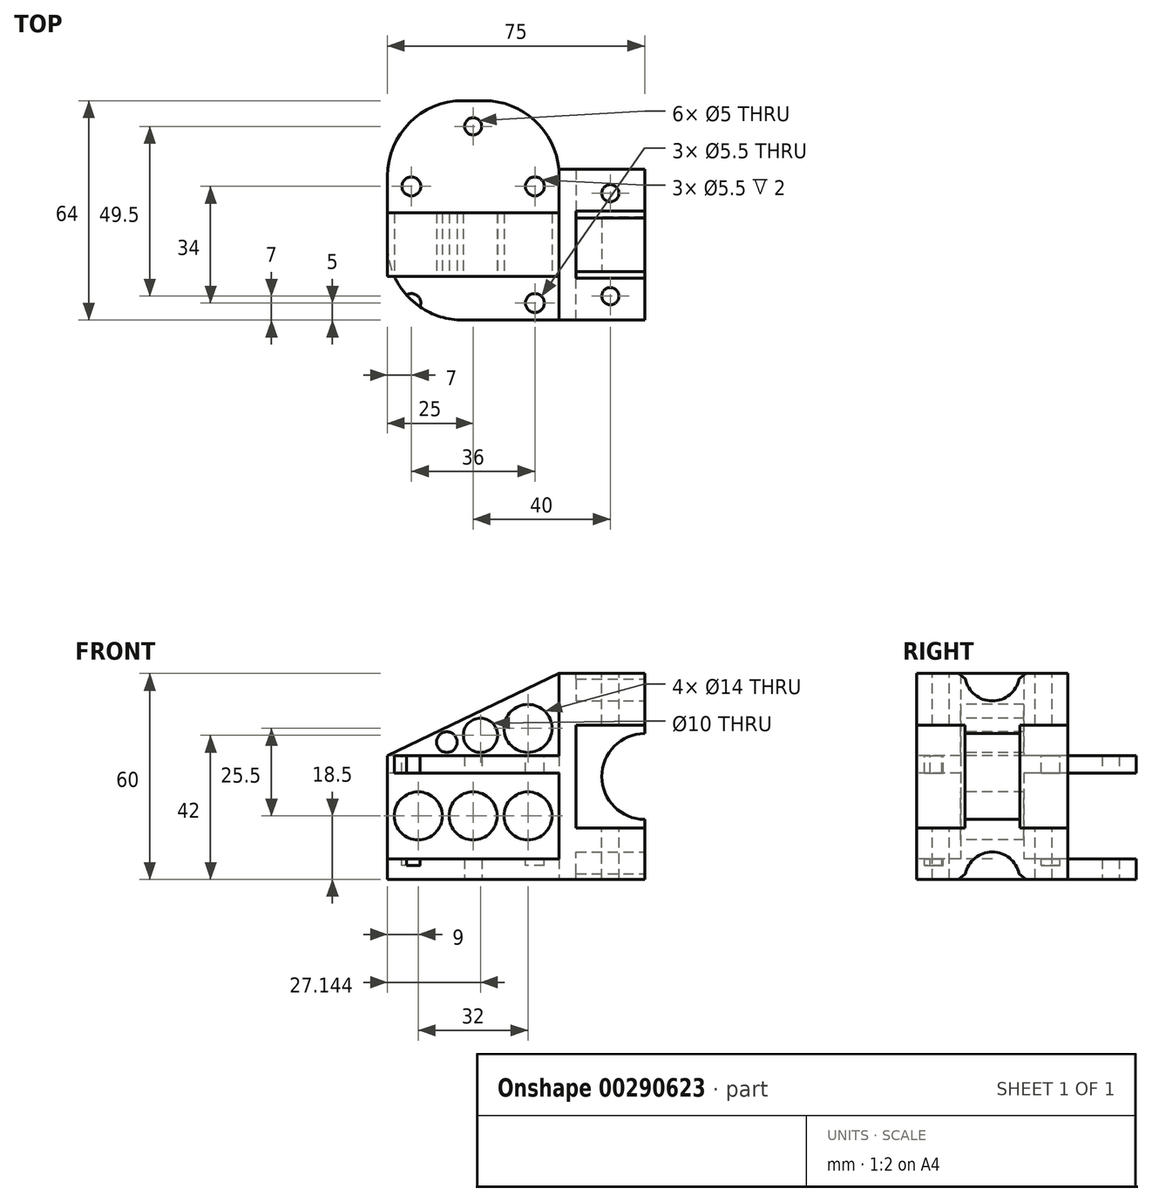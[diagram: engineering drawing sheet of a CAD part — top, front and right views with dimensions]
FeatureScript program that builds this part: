
annotation { "Feature Type Name" : "Feature", "Feature Type Description" : "" }
export const myFeature = defineFeature(function(context is Context, id is Id, definition is map)
    precondition{}
    {
        {
            var Q0;
            Q0=qCreatedBy(makeId("Top.planeOp"),FACE);
            var sketch = newSketch(context, id + "F0", { "sketchPlane" : qUnion([Q0])});
            skLineSegment(sketch, "E0.bottom", {"start": v(-25, 22) * mm, "end": v(25, 22) * mm});
            skLineSegment(sketch, "E0.top", {"start": v(-25, -22) * mm, "end": v(25, -22) * mm});
            skLineSegment(sketch, "E0.left", {"start": v(-25, 22) * mm, "end": v(-25, -22) * mm});
            skLineSegment(sketch, "E0.right", {"start": v(25, 22) * mm, "end": v(25, -22) * mm});
            skLineSegment(sketch, "E1.bottom", {"start": v(25, 22) * mm, "end": v(50, 22) * mm});
            skLineSegment(sketch, "E1.top", {"start": v(25, -22) * mm, "end": v(50, -22) * mm});
            skLineSegment(sketch, "E1.right", {"start": v(50, 22) * mm, "end": v(50, -22) * mm});
            skLineSegment(sketch, "E2", {"start": v(0, 22) * mm, "end": v(0, -22) * mm, "construction": true});
            skLineSegment(sketch, "E3", {"start": v(-25, 0) * mm, "end": v(25, 0) * mm, "construction": true});
            skPoint(sketch, "E4.center.orphan", {"position": v(0, -12) * mm});
            skLineSegment(sketch, "E5.bottom", {"start": v(25, -22) * mm, "end": v(-25, -22) * mm});
            skLineSegment(sketch, "E5.top", {"start": v(25, -42) * mm, "end": v(-25, -42) * mm});
            skLineSegment(sketch, "E5.left", {"start": v(25, -22) * mm, "end": v(25, -42) * mm});
            skLineSegment(sketch, "E5.right", {"start": v(-25, -22) * mm, "end": v(-25, -42) * mm});
            skLineSegment(sketch, "E6.top", {"start": v(-25, 42) * mm, "end": v(25, 42) * mm});
            skLineSegment(sketch, "E6.left", {"start": v(-25, 22) * mm, "end": v(-25, 42) * mm});
            skLineSegment(sketch, "E6.right", {"start": v(25, 22) * mm, "end": v(25, 42) * mm});
            skLineSegment(sketch, "E7", {"start": v(-25, -32) * mm, "end": v(25, -32) * mm, "construction": true});
            skLineSegment(sketch, "E8", {"start": v(0, -22) * mm, "end": v(0, -42) * mm, "construction": true});
            skLineSegment(sketch, "E9", {"start": v(0, 22) * mm, "end": v(0, 42) * mm, "construction": true});
            skLineSegment(sketch, "E10", {"start": v(-25, 32) * mm, "end": v(25, 32) * mm, "construction": true});
            skCircle(sketch, "E11", {"center": v(0, -34.5) * mm, "radius": 2.5 * mm});
            skCircle(sketch, "E12", {"center": v(0, 34.5) * mm, "radius": 2.5 * mm});
            skSolve(sketch);
        }
        {
            var Q0;
            Q0=makeQuery(id+"F0.imprint","IMPRINT",FACE,{"disambiguationData":[TD([[makeQuery(id+"F0.imprint","IMPRINT",EDGE,{"derivedFrom":sQuery(id+"F0.wireOp",EDGE,"E1.bottom")}),-1.0]])]});
            extrude(context, id + "F1", {"entities" : qUnion([Q0]), "depth" : 60 * mm});
        }
        {
            var Q0;
            {var subQ1=sQuery(id+"F0.wireOp",EDGE,"E0.bottom");Q0=makeQuery(id+"F0.imprint","IMPRINT",FACE,{"disambiguationData":[TD([[makeQuery(id+"F0.imprint","IMPRINT",EDGE,{"derivedFrom":subQ1}),-1.0]])]});}
            var Q1;
            Q1=makeQuery(id+"F0.imprint","IMPRINT",FACE,{"disambiguationData":[TD([[makeQuery(id+"F0.imprint","IMPRINT",EDGE,{"derivedFrom":sQuery(id+"F0.wireOp",EDGE,"E0.bottom")}),1.0]])]});
            var Q2;
            Q2=makeQuery(id+"F0.imprint","IMPRINT",FACE,{"disambiguationData":[TD([[makeQuery(id+"F0.imprint","IMPRINT",EDGE,{"derivedFrom":sQuery(id+"F0.wireOp",EDGE,"E5.bottom")}),1.0]])]});
            var Q3;
            Q3=makeQuery(id+"F0.imprint","IMPRINT",FACE,{"disambiguationData":[TD([[makeQuery(id+"F0.imprint","IMPRINT",EDGE,{"derivedFrom":sQuery(id+"F0.wireOp",EDGE,"E0.left")}),1.0]])]});
            extrude(context, id + "F2", {"entities" : qUnion([Q0, Q1, Q2, Q3]), "operationType" : NewBodyOperationType.ADD, "depth" : 6 * mm});
        }
        {
            var Q0;
            Q0=makeQuery(id+"F1.opExtrude","SWEPT_FACE",FACE,{"disambiguationData":[OSD([sQuery(id+"F0.wireOp",EDGE,"E1.right")])]});
            var sketch = newSketch(context, id + "F3", { "sketchPlane" : qUnion([Q0])});
            skCircle(sketch, "E13", {"center": v(0, 0) * mm, "radius": 8 * mm});
            skCircle(sketch, "E14", {"center": v(0, 60) * mm, "radius": 8 * mm});
            skSolve(sketch);
        }
        {
            var Q0;
            Q0 = qSketchRegion(id + "F3", true);
            extrude(context, id + "F4", {"entities" : qUnion([Q0]), "operationType" : NewBodyOperationType.REMOVE, "oppositeDirection" : true, "depth" : 20 * mm});
        }
        {
            var Q0;
            Q0=makeQuery(id+"F1.opExtrude","CAP_FACE",FACE,{"disambiguationData":[OSD([sQuery(id+"F0.wireOp",EDGE,"E1.bottom"),sQuery(id+"F0.wireOp",EDGE,"E1.top"),sQuery(id+"F0.wireOp",EDGE,"E0.right"),sQuery(id+"F0.wireOp",EDGE,"E1.right")])],"isStart":false});
            var sketch = newSketch(context, id + "F5", { "sketchPlane" : qUnion([Q0])});
            skLineSegment(sketch, "E15.bottom", {"start": v(50, 22) * mm, "end": v(30, 22) * mm, "construction": true});
            skLineSegment(sketch, "E15.top", {"start": v(50, -22) * mm, "end": v(30, -22) * mm, "construction": true});
            skLineSegment(sketch, "E15.left", {"start": v(50, 22) * mm, "end": v(50, -22) * mm, "construction": true});
            skLineSegment(sketch, "E15.right", {"start": v(30, 22) * mm, "end": v(30, 8) * mm, "construction": true});
            skLineSegment(sketch, "E16", {"start": v(40, 22) * mm, "end": v(40, 8) * mm, "construction": true});
            skLineSegment(sketch, "E17", {"start": v(30, 8) * mm, "end": v(50, 8) * mm, "construction": true});
            skLineSegment(sketch, "E18", {"start": v(30, -8) * mm, "end": v(50, -8) * mm, "construction": true});
            skLineSegment(sketch, "E19.trimOffspring", {"start": v(40, -8) * mm, "end": v(40, -22) * mm, "construction": true});
            skLineSegment(sketch, "E20.trimOffspring", {"start": v(30, -8) * mm, "end": v(30, -22) * mm, "construction": true});
            skLineSegment(sketch, "E21", {"start": v(30, 15) * mm, "end": v(50, 15) * mm, "construction": true});
            skLineSegment(sketch, "E22", {"start": v(30, -15) * mm, "end": v(50, -15) * mm, "construction": true});
            skCircle(sketch, "E23", {"center": v(40, 15) * mm, "radius": 2.5 * mm});
            skCircle(sketch, "E24", {"center": v(40, -15) * mm, "radius": 2.5 * mm});
            skSolve(sketch);
        }
        {
            var Q0;
            Q0 = qSketchRegion(id + "F5", true);
            extrude(context, id + "F6", {"entities" : qUnion([Q0]), "operationType" : NewBodyOperationType.REMOVE, "oppositeDirection" : true, "depth" : 60 * mm});
        }
        {
            var Q0;
            Q0=makeQuery(id+"F1.opExtrude","SWEPT_FACE",FACE,{"disambiguationData":[OSD([sQuery(id+"F0.wireOp",EDGE,"E1.right")])]});
            var sketch = newSketch(context, id + "F7", { "sketchPlane" : qUnion([Q0])});
            skLineSegment(sketch, "E25.bottom", {"start": v(22, 30) * mm, "end": v(-22, 30) * mm, "construction": true});
            skLineSegment(sketch, "E25.top", {"start": v(22, 30) * mm, "end": v(-22, 30) * mm, "construction": true});
            skLineSegment(sketch, "E25.left", {"start": v(22, 30) * mm, "end": v(22, 30) * mm});
            skLineSegment(sketch, "E25.right", {"start": v(-22, 30) * mm, "end": v(-22, 30) * mm});
            skLineSegment(sketch, "E26.bottom", {"start": v(-22, 45) * mm, "end": v(-8, 45) * mm});
            skLineSegment(sketch, "E26.top", {"start": v(-22, 15) * mm, "end": v(-8, 15) * mm});
            skLineSegment(sketch, "E26.left", {"start": v(-22, 45) * mm, "end": v(-22, 15) * mm});
            skLineSegment(sketch, "E26.right", {"start": v(-8, 45) * mm, "end": v(-8, 15) * mm});
            skLineSegment(sketch, "E27.bottom", {"start": v(22, 45) * mm, "end": v(8, 45) * mm});
            skLineSegment(sketch, "E27.top", {"start": v(22, 15) * mm, "end": v(8, 15) * mm});
            skLineSegment(sketch, "E27.left", {"start": v(22, 45) * mm, "end": v(22, 15) * mm});
            skLineSegment(sketch, "E27.right", {"start": v(8, 45) * mm, "end": v(8, 15) * mm});
            skSolve(sketch);
        }
        {
            var Q0;
            Q0 = qSketchRegion(id + "F7", true);
            extrude(context, id + "F8", {"entities" : qUnion([Q0]), "operationType" : NewBodyOperationType.REMOVE, "oppositeDirection" : true, "depth" : 20 * mm});
        }
        {
            var Q0;
            Q0=makeQuery(id+"F2.opExtrude","CAP_FACE",FACE,{"disambiguationData":[OSD([sQuery(id+"F0.wireOp",EDGE,"E0.bottom"),sQuery(id+"F0.wireOp",EDGE,"E0.top"),sQuery(id+"F0.wireOp",EDGE,"E0.left"),sQuery(id+"F0.wireOp",EDGE,"E0.right"),sQuery(id+"F0.wireOp",EDGE,"CU1M1yZN-sxm3-3OR8-gPQy-L78A4Of9dSzU"),sQuery(id+"F0.wireOp",EDGE,"da8ced7d-3d86-45b0-b41d-8282a98df76d0.MirrorC")])],"isStart":false});
            extrude(context, id + "F9", {"entities" : qUnion([Q0]), "operationType" : NewBodyOperationType.ADD, "depth" : 30 * mm, "hasSecondDirection" : true, "secondDirectionOppositeDirection" : false, "secondDirectionDepth" : 25 * mm});
        }
        {
            var Q0;
            Q0=makeQuery(id+"F9.opExtrude","SWEPT_EDGE",EDGE,{"disambiguationData":[OSD([sQuery(id+"F0.wireOp",EDGE,"E5.top"),sQuery(id+"F0.wireOp",EDGE,"E5.left")])]});
            var Q1;
            Q1=makeQuery(id+"F2.opExtrude","SWEPT_EDGE",EDGE,{"disambiguationData":[OSD([sQuery(id+"F0.wireOp",EDGE,"E5.top"),sQuery(id+"F0.wireOp",EDGE,"E5.left")])]});
            var Q2;
            Q2=makeQuery(id+"F2.opExtrude","SWEPT_EDGE",EDGE,{"disambiguationData":[OSD([sQuery(id+"F0.wireOp",EDGE,"E5.top"),sQuery(id+"F0.wireOp",EDGE,"E5.right")])]});
            var Q3;
            Q3=makeQuery(id+"F9.opExtrude","SWEPT_EDGE",EDGE,{"disambiguationData":[OSD([sQuery(id+"F0.wireOp",EDGE,"E5.top"),sQuery(id+"F0.wireOp",EDGE,"E5.right")])]});
            var Q4;
            Q4=makeQuery(id+"F9.opExtrude","SWEPT_EDGE",EDGE,{"disambiguationData":[OSD([sQuery(id+"F0.wireOp",EDGE,"E6.top"),sQuery(id+"F0.wireOp",EDGE,"E6.left")])]});
            var Q5;
            Q5=makeQuery(id+"F2.opExtrude","SWEPT_EDGE",EDGE,{"disambiguationData":[OSD([sQuery(id+"F0.wireOp",EDGE,"E6.top"),sQuery(id+"F0.wireOp",EDGE,"E6.left")])]});
            var Q6;
            Q6=makeQuery(id+"F9.opExtrude","SWEPT_EDGE",EDGE,{"disambiguationData":[OSD([sQuery(id+"F0.wireOp",EDGE,"E6.top"),sQuery(id+"F0.wireOp",EDGE,"E6.right")])]});
            var Q7;
            Q7=makeQuery(id+"F2.opExtrude","SWEPT_EDGE",EDGE,{"disambiguationData":[OSD([sQuery(id+"F0.wireOp",EDGE,"E6.top"),sQuery(id+"F0.wireOp",EDGE,"E6.right")])]});
            fillet(context, id + "F10", {"entities" : qUnion([Q0, Q1, Q2, Q3, Q4, Q5, Q6, Q7]), "radius" : 22 * mm, "tangentPropagation" : true, "allowEdgeOverflow" : false});
        }
        {
            var Q0;
            Q0=makeQuery(id+"F9.opExtrude","CAP_FACE",FACE,{"disambiguationData":[OSD([sQuery(id+"F0.wireOp",EDGE,"E0.left"),sQuery(id+"F0.wireOp",EDGE,"E0.right"),sQuery(id+"F0.wireOp",EDGE,"E5.top"),sQuery(id+"F0.wireOp",EDGE,"E5.left"),sQuery(id+"F0.wireOp",EDGE,"E5.right"),sQuery(id+"F0.wireOp",EDGE,"E6.top"),sQuery(id+"F0.wireOp",EDGE,"E6.left"),sQuery(id+"F0.wireOp",EDGE,"E6.right"),sQuery(id+"F0.wireOp",EDGE,"E11"),sQuery(id+"F0.wireOp",EDGE,"E12")])],"isStart":false});
            var sketch = newSketch(context, id + "F11", { "sketchPlane" : qUnion([Q0])});
            skCircle(sketch, "E28", {"center": v(18, 17) * mm, "radius": 2.75 * mm});
            skCircle(sketch, "E29.MirrorC", {"center": v(-18, 17) * mm, "radius": 2.75 * mm});
            skCircle(sketch, "E30.MirrorC", {"center": v(-18, -17) * mm, "radius": 2.75 * mm});
            skCircle(sketch, "E31.MirrorC", {"center": v(18, -17) * mm, "radius": 2.75 * mm});
            skSolve(sketch);
        }
        {
            var Q0;
            Q0 = qSketchRegion(id + "F11", true);
            extrude(context, id + "F12", {"entities" : qUnion([Q0]), "operationType" : NewBodyOperationType.REMOVE, "oppositeDirection" : true, "depth" : 32 * mm});
        }
        {
            var Q0;
            Q0=makeQuery(id+"F2.opExtrude","CAP_FACE",FACE,{"disambiguationData":[OSD([sQuery(id+"F0.wireOp",EDGE,"E0.left"),sQuery(id+"F0.wireOp",EDGE,"E0.right"),sQuery(id+"F0.wireOp",EDGE,"E5.top"),sQuery(id+"F0.wireOp",EDGE,"E5.left"),sQuery(id+"F0.wireOp",EDGE,"E5.right"),sQuery(id+"F0.wireOp",EDGE,"E6.top"),sQuery(id+"F0.wireOp",EDGE,"E6.left"),sQuery(id+"F0.wireOp",EDGE,"E6.right"),sQuery(id+"F0.wireOp",EDGE,"E11"),sQuery(id+"F0.wireOp",EDGE,"E12")])],"isStart":false});
            var sketch = newSketch(context, id + "F13", { "sketchPlane" : qUnion([Q0])});
            skLineSegment(sketch, "E32.bottom", {"start": v(25, 9.25) * mm, "end": v(-25, 9.25) * mm});
            skLineSegment(sketch, "E32.top", {"start": v(25, -9.25) * mm, "end": v(-25, -9.25) * mm});
            skLineSegment(sketch, "E32.left", {"start": v(25, 9.25) * mm, "end": v(25, -9.25) * mm});
            skLineSegment(sketch, "E32.right", {"start": v(-25, 9.25) * mm, "end": v(-25, -9.25) * mm});
            skSolve(sketch);
        }
        {
            var Q0;
            Q0 = qSketchRegion(id + "F13", true);
            extrude(context, id + "F14", {"entities" : qUnion([Q0]), "operationType" : NewBodyOperationType.ADD, "depth" : 54 * mm});
        }
        {
            var Q0;
            {var subQ4=sQuery(id+"F0.wireOp",EDGE,"E0.right");var subQ5=sQuery(id+"F13.wireOp",EDGE,"E32.top");Q0=makeQuery(id+"F14.boolean.opBoolean","SPLIT",FACE,{"disambiguationData":[TD([makeQuery(id+"F1.opExtrude","CAP_FACE",FACE,{"disambiguationData":[OSD([sQuery(id+"F0.wireOp",EDGE,"E1.bottom"),sQuery(id+"F0.wireOp",EDGE,"E1.top"),subQ4,sQuery(id+"F0.wireOp",EDGE,"E1.right")])],"isStart":false})])],"derivedFrom":makeQuery(id+"F14.opExtrude","SWEPT_FACE",FACE,{"disambiguationData":[OSD([subQ5])]})});}
            var sketch = newSketch(context, id + "F15", { "sketchPlane" : qUnion([Q0])});
            skLineSegment(sketch, "E33", {"start": v(25, 60) * mm, "end": v(-25, 36) * mm});
            skLineSegment(sketch, "E34", {"start": v(-25, 36) * mm, "end": v(-25, 60) * mm});
            skLineSegment(sketch, "E35", {"start": v(-25, 60) * mm, "end": v(25, 60) * mm});
            skSolve(sketch);
        }
        {
            var Q0;
            Q0 = qSketchRegion(id + "F15", true);
            extrude(context, id + "F16", {"entities" : qUnion([Q0]), "operationType" : NewBodyOperationType.REMOVE, "oppositeDirection" : true, "depth" : 18.5 * mm});
        }
        {
            var Q0;
            Q0=makeQuery(id+"F8.boolean.opBoolean","COPY",FACE,{"derivedFrom":makeQuery(id+"F8.opExtrude","SWEPT_FACE",FACE,{"disambiguationData":[OSD([sQuery(id+"F7.wireOp",EDGE,"E26.right")])]})});
            var sketch = newSketch(context, id + "F17", { "sketchPlane" : qUnion([Q0])});
            skCircle(sketch, "E36", {"center": v(50, 30) * mm, "radius": 12.5 * mm});
            skSolve(sketch);
        }
        {
            var Q0;
            Q0 = qSketchRegion(id + "F17", true);
            extrude(context, id + "F18", {"entities" : qUnion([Q0]), "operationType" : NewBodyOperationType.REMOVE, "oppositeDirection" : true, "depth" : 16.8 * mm});
        }
        {
            var Q0;
            {var subQ0=sQuery(id+"F0.wireOp",EDGE,"E6.left");var subQ1=sQuery(id+"F0.wireOp",EDGE,"E5.right");var subQ2=sQuery(id+"F0.wireOp",EDGE,"E0.left");var subQ3=sQuery(id+"F0.wireOp",EDGE,"E12");var subQ4=sQuery(id+"F0.wireOp",EDGE,"E11");var subQ5=sQuery(id+"F0.wireOp",EDGE,"E6.right");var subQ6=sQuery(id+"F0.wireOp",EDGE,"E6.top");var subQ7=sQuery(id+"F0.wireOp",EDGE,"E5.left");var subQ8=sQuery(id+"F0.wireOp",EDGE,"E5.top");var subQ9=sQuery(id+"F0.wireOp",EDGE,"E0.right");Q0=makeQuery(id+"F14.boolean.opBoolean","SPLIT",FACE,{"disambiguationData":[TD([makeQuery(id+"F2.opExtrude","CAP_FACE",FACE,{"disambiguationData":[OSD([subQ2,subQ9,subQ8,subQ7,subQ1,subQ6,subQ0,subQ5,subQ4,subQ3])],"isStart":false})])],"derivedFrom":makeQuery(id+"F14.opExtrude","SWEPT_FACE",FACE,{"disambiguationData":[OSD([sQuery(id+"F13.wireOp",EDGE,"E32.top")])]})});}
            var sketch = newSketch(context, id + "F19", { "sketchPlane" : qUnion([Q0])});
            skLineSegment(sketch, "E37", {"start": v(0, 31) * mm, "end": v(0, 6) * mm, "construction": true});
            skLineSegment(sketch, "E38", {"start": v(-25, 18.5) * mm, "end": v(25, 18.5) * mm, "construction": true});
            skCircle(sketch, "E39", {"center": v(0, 18.5) * mm, "radius": 7 * mm});
            skCircle(sketch, "E40", {"center": v(16, 18.5) * mm, "radius": 7 * mm});
            skCircle(sketch, "E41", {"center": v(-16, 18.5) * mm, "radius": 7 * mm});
            skSolve(sketch);
        }
        {
            var Q0;
            Q0 = qSketchRegion(id + "F19", true);
            extrude(context, id + "F20", {"entities" : qUnion([Q0]), "operationType" : NewBodyOperationType.REMOVE, "oppositeDirection" : true, "depth" : 18.5 * mm});
        }
        {
            var Q0;
            {var subQ4=sQuery(id+"F0.wireOp",EDGE,"E0.right");var subQ5=sQuery(id+"F13.wireOp",EDGE,"E32.top");Q0=makeQuery(id+"F14.boolean.opBoolean","SPLIT",FACE,{"disambiguationData":[TD([makeQuery(id+"F1.opExtrude","CAP_FACE",FACE,{"disambiguationData":[OSD([sQuery(id+"F0.wireOp",EDGE,"E1.bottom"),sQuery(id+"F0.wireOp",EDGE,"E1.top"),subQ4,sQuery(id+"F0.wireOp",EDGE,"E1.right")])],"isStart":false})])],"derivedFrom":makeQuery(id+"F14.opExtrude","SWEPT_FACE",FACE,{"disambiguationData":[OSD([subQ5])]})});}
            var sketch = newSketch(context, id + "F21", { "sketchPlane" : qUnion([Q0])});
            skCircle(sketch, "E42", {"center": v(16, 44) * mm, "radius": 7 * mm});
            skCircle(sketch, "E43", {"center": v(-7.65, 40) * mm, "radius": 3 * mm});
            skCircle(sketch, "E44", {"center": v(2.14, 42) * mm, "radius": 5 * mm});
            skSolve(sketch);
        }
        {
            var Q0;
            Q0 = qSketchRegion(id + "F21", true);
            extrude(context, id + "F22", {"entities" : qUnion([Q0]), "operationType" : NewBodyOperationType.REMOVE, "oppositeDirection" : true, "depth" : 18.5 * mm});
        }
        {
            var Q0;
            Q0=makeQuery(id+"F4.boolean.opBoolean","INTERSECT",EDGE,{"disambiguationData":[OD(0.0)],"derivedFrom":[makeQuery(id+"F1.opExtrude","CAP_FACE",FACE,{"disambiguationData":[OSD([sQuery(id+"F0.wireOp",EDGE,"E1.bottom"),sQuery(id+"F0.wireOp",EDGE,"E1.top"),sQuery(id+"F0.wireOp",EDGE,"E0.right"),sQuery(id+"F0.wireOp",EDGE,"E1.right")])],"isStart":false}),makeQuery(id+"F4.opExtrude","SWEPT_FACE",FACE,{"disambiguationData":[OSD([sQuery(id+"F3.wireOp",EDGE,"E14")])]})]});
            var Q1;
            Q1=makeQuery(id+"F4.boolean.opBoolean","INTERSECT",EDGE,{"disambiguationData":[OD(1.0)],"derivedFrom":[makeQuery(id+"F1.opExtrude","CAP_FACE",FACE,{"disambiguationData":[OSD([sQuery(id+"F0.wireOp",EDGE,"E1.bottom"),sQuery(id+"F0.wireOp",EDGE,"E1.top"),sQuery(id+"F0.wireOp",EDGE,"E0.right"),sQuery(id+"F0.wireOp",EDGE,"E1.right")])],"isStart":false}),makeQuery(id+"F4.opExtrude","SWEPT_FACE",FACE,{"disambiguationData":[OSD([sQuery(id+"F3.wireOp",EDGE,"E14")])]})]});
            var Q2;
            {var subQ0=sQuery(id+"F0.wireOp",EDGE,"E0.right");Q2=makeQuery(id+"F4.boolean.opBoolean","INTERSECT",EDGE,{"disambiguationData":[OD(0.0)],"derivedFrom":[makeQuery(id+"F2.boolean.opBoolean","MERGE",FACE,{"derivedFrom":[makeQuery(id+"F1.opExtrude","CAP_FACE",FACE,{"disambiguationData":[OSD([sQuery(id+"F0.wireOp",EDGE,"E1.bottom"),sQuery(id+"F0.wireOp",EDGE,"E1.top"),subQ0,sQuery(id+"F0.wireOp",EDGE,"E1.right")])],"isStart":true}),makeQuery(id+"F2.opExtrude","CAP_FACE",FACE,{"disambiguationData":[OSD([sQuery(id+"F0.wireOp",EDGE,"E0.left"),subQ0,sQuery(id+"F0.wireOp",EDGE,"E5.top"),sQuery(id+"F0.wireOp",EDGE,"E5.left"),sQuery(id+"F0.wireOp",EDGE,"E5.right"),sQuery(id+"F0.wireOp",EDGE,"E6.top"),sQuery(id+"F0.wireOp",EDGE,"E6.left"),sQuery(id+"F0.wireOp",EDGE,"E6.right"),sQuery(id+"F0.wireOp",EDGE,"E11"),sQuery(id+"F0.wireOp",EDGE,"E12")])],"isStart":true})]}),makeQuery(id+"F4.opExtrude","SWEPT_FACE",FACE,{"disambiguationData":[OSD([sQuery(id+"F3.wireOp",EDGE,"E13")])]})]});}
            var Q3;
            {var subQ0=sQuery(id+"F0.wireOp",EDGE,"E0.right");Q3=makeQuery(id+"F4.boolean.opBoolean","INTERSECT",EDGE,{"disambiguationData":[OD(1.0)],"derivedFrom":[makeQuery(id+"F2.boolean.opBoolean","MERGE",FACE,{"derivedFrom":[makeQuery(id+"F1.opExtrude","CAP_FACE",FACE,{"disambiguationData":[OSD([sQuery(id+"F0.wireOp",EDGE,"E1.bottom"),sQuery(id+"F0.wireOp",EDGE,"E1.top"),subQ0,sQuery(id+"F0.wireOp",EDGE,"E1.right")])],"isStart":true}),makeQuery(id+"F2.opExtrude","CAP_FACE",FACE,{"disambiguationData":[OSD([sQuery(id+"F0.wireOp",EDGE,"E0.left"),subQ0,sQuery(id+"F0.wireOp",EDGE,"E5.top"),sQuery(id+"F0.wireOp",EDGE,"E5.left"),sQuery(id+"F0.wireOp",EDGE,"E5.right"),sQuery(id+"F0.wireOp",EDGE,"E6.top"),sQuery(id+"F0.wireOp",EDGE,"E6.left"),sQuery(id+"F0.wireOp",EDGE,"E6.right"),sQuery(id+"F0.wireOp",EDGE,"E11"),sQuery(id+"F0.wireOp",EDGE,"E12")])],"isStart":true})]}),makeQuery(id+"F4.opExtrude","SWEPT_FACE",FACE,{"disambiguationData":[OSD([sQuery(id+"F3.wireOp",EDGE,"E13")])]})]});}
            chamfer(context, id + "F23", {"entities" : qUnion([Q0, Q1, Q2, Q3]), "width" : 2 * mm, "tangentPropagation" : true});
        }
    });
